# Revit family: Door-Slider-Fleetwood-3070-OXX
name_source: partatom
category: Doors
revit_build: Autodesk Revit Architecture 2013 (Build: 20120221_2030(x64)
units: mm (PartAtom-declared; Revit-internal decimal feet)

## types (6) — shared parameters
Analytic Construction = <None>
Centerline_1_Calc = 3' - 4"
Centerline_2_Calc = 3' - 4"
Configuration = OXX
Custom_Centerline_1 = 0' - 0"
Custom_Centerline_2 = 0' - 0"
Equal_Centerlines = Yes
Exterior Wrap Overhang = 0' - 0 1/2"
Frame_&_Panel = Aluminum, Anodized Clear
Function = Exterior
Glazing = Glass
Hardware = Stainless Steel, Brushed
Height = 8' - 0"
Interior Wrap Overhang = 0' - 0 1/2"
Manufacturer = Fleetwood Windows and Doors
Model = 3070
Number_Of_Tracks = 3
Panel_1 = 3' - 4 9/32"
Panel_2 = 3' - 4 1/16"
Panel_2_Configuration = 3070_EX_Panel : Sliding Panel  Interlock and Interlock
Panel_3 = 3' - 6 1/16"
Rough Height = 8' - 0 1/4"
Rough Width = 10' - 0 1/2"
Thickness = 0' - 5 23/32"
URL = www.fleetwoodusa.com
Wall Closure = By host
Width = 10' - 0"

## per-type parameters (varying)
| type | Actuator_Height | Panel_1_Configuration | Panel_3_Configuration |
| Archetype Hardware_Archetype Narrow Fixed Stile | 4' - 5 3/4" | 3070_EX_Panel : Fixed Panel Archetype Narrow Stile | 3070_EX_Panel : Active Lead Panel Right Archetype |
| Archetype Hardware_Archetype Fixed Stile | 4' - 5 3/4" | 3070_EX_Panel : Fixed Panel Archetype Stile | 3070_EX_Panel : Active Lead Panel Right Archetype |
| Archetype Narrow Hardware_Narrow Fixed Stile | 3' - 10" | 3070_EX_Panel : Fixed Panel Narrow Fixed Stile | 3070_EX_Panel : Active Lead Panel Right Archetype Narrow |
| Archetype Narrow Hardware_Archetype Narrow Fixed Stile | 3' - 10" | 3070_EX_Panel : Fixed Panel Archetype Narrow Stile | 3070_EX_Panel : Active Lead Panel Right Archetype Narrow |
| Archetype Narrow Hardware_Archetype Fixed Stile | 3' - 10" | 3070_EX_Panel : Fixed Panel Archetype Stile | 3070_EX_Panel : Active Lead Panel Right Archetype Narrow |
| Archetype Hardware_Narrow Fixed Stile | 4' - 5 3/4" | 3070_EX_Panel : Fixed Panel Narrow Fixed Stile | 3070_EX_Panel : Active Lead Panel Right Archetype |

## geometry (parser evidence)
native form markers: Blend x20, Sweep x17
no freeform markers — native parametric forms only
